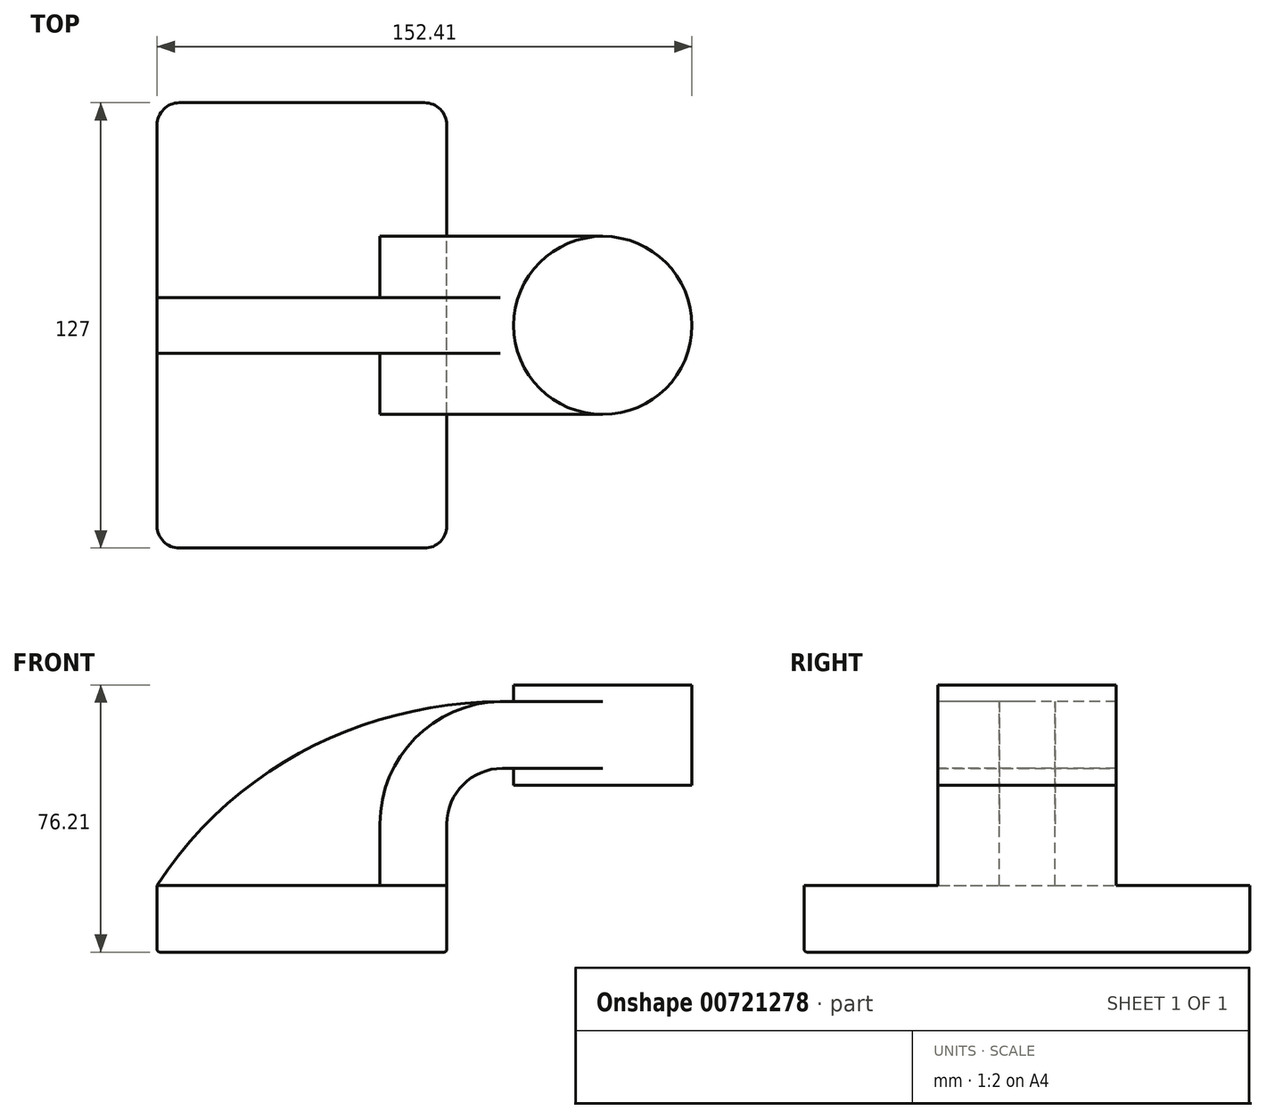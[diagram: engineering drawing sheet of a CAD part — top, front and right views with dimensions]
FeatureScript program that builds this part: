
annotation { "Feature Type Name" : "Feature", "Feature Type Description" : "" }
export const myFeature = defineFeature(function(context is Context, id is Id, definition is map)
    precondition{}
    {
        {
            var Q0;
            Q0=qCreatedBy(makeId("Front.planeOp"),FACE);
            var sketch = newSketch(context, id + "F0", { "sketchPlane" : qUnion([Q0])});
            skLineSegment(sketch, "E0.bottom", {"start": v(41.27, 9.53) * mm, "end": v(-41.28, 9.53) * mm});
            skLineSegment(sketch, "E0.top", {"start": v(41.28, -9.52) * mm, "end": v(-41.27, -9.52) * mm});
            skLineSegment(sketch, "E0.left", {"start": v(41.28, 9.53) * mm, "end": v(41.28, -9.52) * mm});
            skLineSegment(sketch, "E0.right", {"start": v(-41.28, 9.53) * mm, "end": v(-41.27, -9.52) * mm});
            skPoint(sketch, "E0.middle", {"position": v(0, 0) * mm});
            skLineSegment(sketch, "E1.bottom", {"start": v(111.12, 66.68) * mm, "end": v(60.32, 66.68) * mm});
            skLineSegment(sketch, "E1.top", {"start": v(111.12, 38.1) * mm, "end": v(60.32, 38.1) * mm});
            skLineSegment(sketch, "E1.left", {"start": v(111.12, 66.68) * mm, "end": v(111.12, 38.1) * mm});
            skLineSegment(sketch, "E1.right", {"start": v(60.32, 66.68) * mm, "end": v(60.32, 38.1) * mm});
            skPoint(sketch, "E1.middle", {"position": v(85.72, 52.39) * mm});
            skLineSegment(sketch, "E2", {"start": v(41.27, 9.53) * mm, "end": v(41.27, 27) * mm});
            skArc(sketch, "E3", {"start": v(41.27, 27) * mm, "mid": v(45.92, 38.23) * mm, "end": v(57.15, 42.88) * mm});
            skLineSegment(sketch, "E4", {"start": v(57.15, 42.88) * mm, "end": v(85.72, 42.88) * mm});
            skLineSegment(sketch, "E5.0", {"start": v(57.15, 61.93) * mm, "end": v(85.72, 61.93) * mm});
            skArc(sketch, "E5.1", {"start": v(22.23, 27) * mm, "mid": v(32.45, 51.7) * mm, "end": v(57.15, 61.93) * mm});
            skLineSegment(sketch, "E5.2", {"start": v(22.22, 9.53) * mm, "end": v(22.22, 27) * mm});
            skLineSegment(sketch, "E6", {"start": v(85.72, 38.1) * mm, "end": v(85.73, 66.68) * mm});
            skFitSpline(sketch, "E7", {"points": [v(-41.28, 9.52) * mm, v(57.15, 61.93) * mm], "startDerivative": vector(66.42, 102.58) * mm, "endDerivative": vector(117.04, 0.78) * mm});
            skSolve(sketch);
        }
        {
            var Q0;
            Q0=makeQuery(id+"F0.imprint","IMPRINT",FACE,{"disambiguationData":[TD([[makeQuery(id+"F0.imprint","IMPRINT",EDGE,{"derivedFrom":sQuery(id+"F0.wireOp",EDGE,"E0.top")}),-1.0]])]});
            extrude(context, id + "F1", {"entities" : qUnion([Q0]), "endBound" : BoundingType.SYMMETRIC, "depth" : 127 * mm, "offsetDistance" : 25.4 * mm});
        }
        {
            var Q0;
            {var subQ1=sQuery(id+"F0.wireOp",EDGE,"E2");Q0=makeQuery(id+"F0.imprint","IMPRINT",FACE,{"disambiguationData":[TD([[makeQuery(id+"F0.imprint","IMPRINT",EDGE,{"derivedFrom":subQ1}),1.0]])]});}
            var Q1;
            {var subQ0=sQuery(id+"F0.wireOp",EDGE,"E5.0");var subQ1=sQuery(id+"F0.wireOp",EDGE,"E1.right");var subQ2=makeQuery(id+"F0.imprint","INTERSECT",VERTEX,{"derivedFrom":[subQ1,subQ0]});Q1=makeQuery(id+"F0.imprint","IMPRINT",FACE,{"disambiguationData":[TD([[makeQuery(id+"F0.imprint","IMPRINT",EDGE,{"disambiguationData":[TD([[subQ2,-1.0]])],"derivedFrom":subQ1}),1.0]])]});}
            extrude(context, id + "F2", {"entities" : qUnion([Q0, Q1]), "operationType" : NewBodyOperationType.ADD, "endBound" : BoundingType.SYMMETRIC, "depth" : 50.8 * mm, "offsetDistance" : 25.4 * mm});
        }
        {
            var Q0;
            {var subQ3=sQuery(id+"F0.wireOp",EDGE,"E5.2");Q0=makeQuery(id+"F0.imprint","IMPRINT",FACE,{"disambiguationData":[TD([[makeQuery(id+"F0.imprint","IMPRINT",EDGE,{"derivedFrom":subQ3}),1.0]])]});}
            extrude(context, id + "F3", {"entities" : qUnion([Q0]), "operationType" : NewBodyOperationType.ADD, "endBound" : BoundingType.SYMMETRIC, "depth" : 15.88 * mm, "offsetDistance" : 25.4 * mm});
        }
        {
            var Q0;
            {var subQ0=sQuery(id+"F0.wireOp",EDGE,"E1.left");Q0=makeQuery(id+"F0.imprint","IMPRINT",FACE,{"disambiguationData":[TD([[makeQuery(id+"F0.imprint","IMPRINT",EDGE,{"derivedFrom":subQ0}),-1.0]])]});}
            var Q1;
            Q1=sQuery(id+"F0.wireOp",EDGE,"E6");
            revolve(context, id + "F4", {"operationType" : NewBodyOperationType.ADD, "surfaceOperationType" : NewSurfaceOperationType.NEW, "entities" : qUnion([Q0]), "axis" : qUnion([Q1]), "revolveType" : RevolveType.FULL});
        }
        {
            var Q0;
            Q0=makeQuery(id+"F1.opExtrude","CAP_EDGE",EDGE,{"disambiguationData":[OSD([sQuery(id+"F0.wireOp",EDGE,"E0.right")])],"isStart":false});
            var Q1;
            Q1=makeQuery(id+"F1.opExtrude","CAP_EDGE",EDGE,{"disambiguationData":[OSD([sQuery(id+"F0.wireOp",EDGE,"E0.left")])],"isStart":false});
            var Q2;
            Q2=makeQuery(id+"F1.opExtrude","CAP_EDGE",EDGE,{"disambiguationData":[OSD([sQuery(id+"F0.wireOp",EDGE,"E0.left")])],"isStart":true});
            var Q3;
            Q3=makeQuery(id+"F1.opExtrude","CAP_EDGE",EDGE,{"disambiguationData":[OSD([sQuery(id+"F0.wireOp",EDGE,"E0.right")])],"isStart":true});
            fillet(context, id + "F5", {"entities" : qUnion([Q0, Q1, Q2, Q3]), "radius" : 6.35 * mm, "tangentPropagation" : true, "allowEdgeOverflow" : false});
        }
        {
            var Q0;
            Q0=makeQuery(id+"F1.opExtrude","SWEPT_FACE",FACE,{"disambiguationData":[OSD([sQuery(id+"F0.wireOp",EDGE,"E0.top")])]});
            fillet(context, id + "F6", {"entities" : qUnion([Q0]), "radius" : 0.76 * mm, "tangentPropagation" : true, "allowEdgeOverflow" : false});
        }
    });
